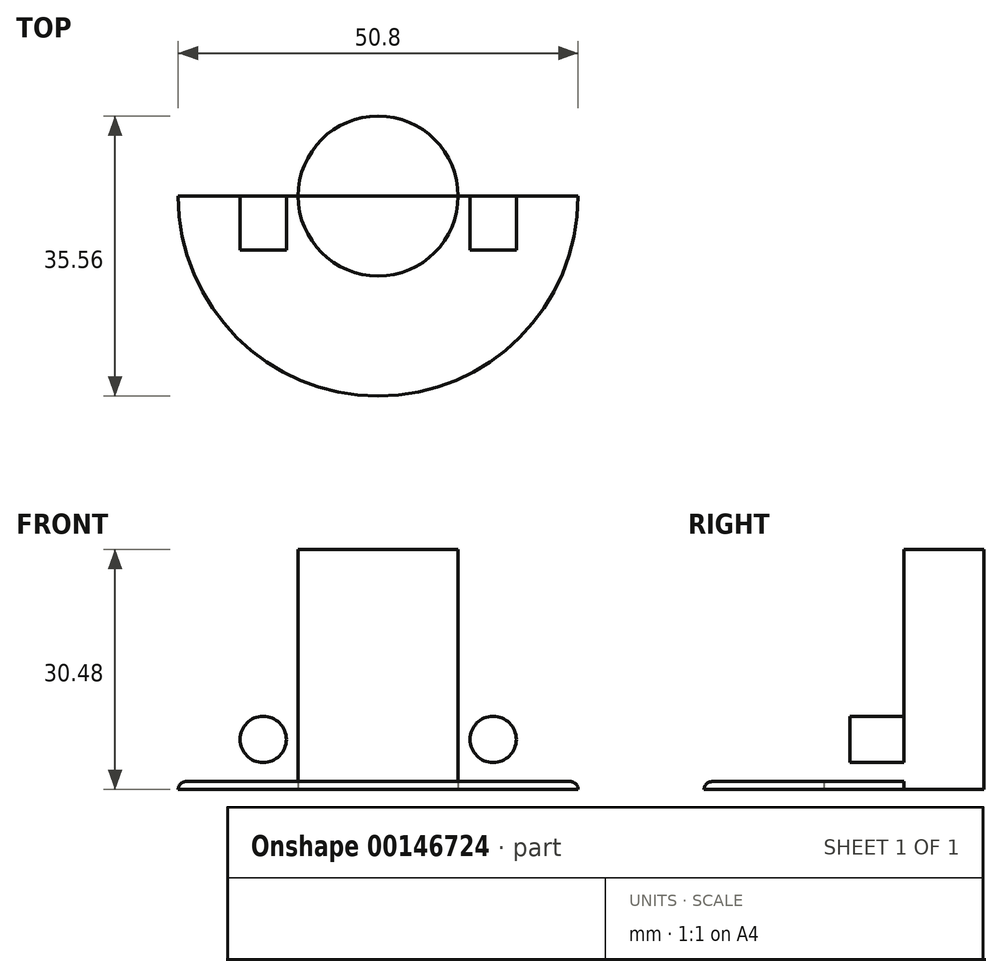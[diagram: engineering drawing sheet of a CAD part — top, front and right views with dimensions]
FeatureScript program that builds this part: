
annotation { "Feature Type Name" : "Feature", "Feature Type Description" : "" }
export const myFeature = defineFeature(function(context is Context, id is Id, definition is map)
    precondition{}
    {
        {
            assignVariable(context, id + "F0", {"name" : "R", "anyValue" : 2});
        }
        {
            var Q0;
            Q0=qCreatedBy(makeId("Top.planeOp"),FACE);
            var sketch = newSketch(context, id + "F1", { "sketchPlane" : qUnion([Q0])});
            skCircle(sketch, "E0", {"center": v(0, 0) * mm, "radius": 25.4 * mm});
            skCircle(sketch, "E1", {"center": v(0, 0) * mm, "radius": 10.16 * mm});
            skLineSegment(sketch, "E2", {"start": v(-25.4, 0) * mm, "end": v(25.4, 0) * mm});
            skSolve(sketch);
        }
        {
            var Q0;
            {var subQ0=sQuery(id+"F1.wireOp",EDGE,"E2");var subQ1=sQuery(id+"F1.wireOp",EDGE,"E0");var subQ2=makeQuery(id+"F1.imprint","INTERSECT",VERTEX,{"disambiguationData":[OD(0.0)],"derivedFrom":[subQ1,subQ0]});Q0=makeQuery(id+"F1.imprint","IMPRINT",FACE,{"disambiguationData":[TD([[makeQuery(id+"F1.imprint","IMPRINT",EDGE,{"disambiguationData":[TD([[subQ2,1.0]])],"derivedFrom":subQ1}),1.0]])]});}
            var Q1;
            {var subQ0=sQuery(id+"F1.wireOp",EDGE,"E2");var subQ1=sQuery(id+"F1.wireOp",EDGE,"E1");var subQ2=makeQuery(id+"F1.imprint","INTERSECT",VERTEX,{"disambiguationData":[OD(0.0)],"derivedFrom":[subQ1,subQ0]});Q1=makeQuery(id+"F1.imprint","IMPRINT",FACE,{"disambiguationData":[TD([[makeQuery(id+"F1.imprint","IMPRINT",EDGE,{"disambiguationData":[TD([[subQ2,1.0]])],"derivedFrom":subQ1}),1.0]])]});}
            extrude(context, id + "F2", {"entities" : qUnion([Q0, Q1]), "depth" : (getVariable(context, 'R') / 2) * mm});
        }
        {
            var Q0;
            Q0=makeQuery(id+"F2.opExtrude","CAP_EDGE",EDGE,{"disambiguationData":[OSD([sQuery(id+"F1.wireOp",EDGE,"E0")])],"isStart":false});
            fillet(context, id + "F3", {"entities" : qUnion([Q0]), "radius" : (getVariable(context, 'R') / 2) * mm, "tangentPropagation" : true, "allowEdgeOverflow" : false});
        }
        {
            var Q0;
            {var subQ0=sQuery(id+"F1.wireOp",EDGE,"E2");var subQ1=sQuery(id+"F1.wireOp",EDGE,"E1");var subQ2=makeQuery(id+"F1.imprint","INTERSECT",VERTEX,{"disambiguationData":[OD(0.0)],"derivedFrom":[subQ1,subQ0]});Q0=makeQuery(id+"F1.imprint","IMPRINT",FACE,{"disambiguationData":[TD([[makeQuery(id+"F1.imprint","IMPRINT",EDGE,{"disambiguationData":[TD([[subQ2,1.0]])],"derivedFrom":subQ1}),1.0]])]});}
            extrude(context, id + "F4", {"entities" : qUnion([Q0]), "operationType" : NewBodyOperationType.ADD, "depth" : 30.48 * mm});
        }
        {
            var Q0;
            Q0=makeQuery(id+"F2.opExtrude","CAP_FACE",FACE,{"disambiguationData":[OSD([sQuery(id+"F1.wireOp",EDGE,"E0"),sQuery(id+"F1.wireOp",EDGE,"E2")])],"isStart":true});
            var sketch = newSketch(context, id + "F5", { "sketchPlane" : qUnion([Q0])});
            skPoint(sketch, "E3", {"position": v(0, 0) * mm});
            skCircle(sketch, "E4", {"center": v(0, 0) * mm, "radius": 6.35 * mm});
            skLineSegment(sketch, "E5", {"start": v(0, 0) * mm, "end": v(-12.7, 0) * mm});
            skLineSegment(sketch, "E6", {"start": v(0, 0) * mm, "end": v(12.7, 0) * mm});
            skCircle(sketch, "E7", {"center": v(-12.7, 0) * mm, "radius": 2.54 * mm});
            skCircle(sketch, "E8", {"center": v(12.7, 0) * mm, "radius": 2.54 * mm});
            skCircle(sketch, "E9", {"center": v(0, 0) * mm, "radius": 3.18 * mm});
            skCircle(sketch, "E10", {"center": v(0, 0) * mm, "radius": 8.26 * mm});
            skSolve(sketch);
        }
        {
            var Q0;
            Q0=sQuery(id+"F5.wireOp",VERTEX,"E3");
            var Q1;
            Q1=makeQuery(id+"F2.opExtrude","SWEPT_BODY",BODY,{"disambiguationData":[OSD([sQuery(id+"F1.wireOp",EDGE,"E0")])]});
            hole(context, id + "F6", {"style" : HoleStyle.SIMPLE, "endStyle" : HoleEndStyle.THROUGH, "holeDiameter" : 16.5 * mm, "startFromSketch" : true, "locations" : qUnion([Q0]), "scope" : qUnion([Q1]), "isTappedThrough" : true});
        }
        {
            var Q0;
            {var subQ0=sQuery(id+"F5.wireOp",EDGE,"E5");var subQ1=sQuery(id+"F5.wireOp",EDGE,"E4");var subQ2=makeQuery(id+"F5.imprint","INTERSECT",VERTEX,{"derivedFrom":[subQ1,subQ0]});Q0=makeQuery(id+"F5.imprint","IMPRINT",FACE,{"disambiguationData":[TD([[makeQuery(id+"F5.imprint","IMPRINT",EDGE,{"disambiguationData":[TD([[subQ2,-1.0]])],"derivedFrom":subQ1}),1.0]])]});}
            var Q1;
            {var subQ0=sQuery(id+"F5.wireOp",EDGE,"E5");var subQ1=sQuery(id+"F5.wireOp",EDGE,"E4");var subQ2=makeQuery(id+"F5.imprint","INTERSECT",VERTEX,{"derivedFrom":[subQ1,subQ0]});Q1=makeQuery(id+"F5.imprint","IMPRINT",FACE,{"disambiguationData":[TD([[makeQuery(id+"F5.imprint","IMPRINT",EDGE,{"disambiguationData":[TD([[subQ2,-1.0]])],"derivedFrom":subQ1}),-1.0]])]});}
            extrude(context, id + "F7", {"entities" : qUnion([Q0, Q1]), "operationType" : NewBodyOperationType.ADD, "oppositeDirection" : true, "depth" : 12.7 * mm});
        }
        {
            var Q0;
            {var subQ0=sQuery(id+"F5.wireOp",EDGE,"E5");var subQ1=sQuery(id+"F5.wireOp",EDGE,"E4");var subQ2=makeQuery(id+"F5.imprint","INTERSECT",VERTEX,{"derivedFrom":[subQ1,subQ0]});Q0=makeQuery(id+"F5.imprint","IMPRINT",FACE,{"disambiguationData":[TD([[makeQuery(id+"F5.imprint","IMPRINT",EDGE,{"disambiguationData":[TD([[subQ2,-1.0]])],"derivedFrom":subQ1}),-1.0]])]});}
            extrude(context, id + "F8", {"entities" : qUnion([Q0]), "operationType" : NewBodyOperationType.ADD, "oppositeDirection" : true, "depth" : 30.48 * mm, "hasSecondDirection" : true, "secondDirectionOppositeDirection" : true, "secondDirectionDepth" : 27.94 * mm});
        }
        {
            var Q0;
            {var subQ0=sQuery(id+"F5.wireOp",EDGE,"E5");var subQ1=sQuery(id+"F1.wireOp",EDGE,"E2");Q0=makeQuery(id+"F8.boolean.opBoolean","MERGE",FACE,{"derivedFrom":[makeQuery(id+"F7.boolean.opBoolean","MERGE",FACE,{"derivedFrom":[makeQuery(id+"F6.hole-0.boolean.opBoolean","SPLIT",FACE,{"disambiguationData":[OD(0.0)],"derivedFrom":makeQuery(id+"F4.boolean.opBoolean","MERGE",FACE,{"derivedFrom":[makeQuery(id+"F2.opExtrude","SWEPT_FACE",FACE,{"disambiguationData":[OSD([subQ1])]}),makeQuery(id+"F4.opExtrude","SWEPT_FACE",FACE,{"disambiguationData":[OSD([subQ1])]})]})}),makeQuery(id+"F7.opExtrude","SWEPT_FACE",FACE,{"disambiguationData":[OSD([subQ0])]})]}),makeQuery(id+"F8.opExtrude","SWEPT_FACE",FACE,{"disambiguationData":[OSD([subQ0])]})]});}
            var sketch = newSketch(context, id + "F11", { "sketchPlane" : qUnion([Q0])});
            skLineSegment(sketch, "E11", {"start": v(-8.26, 12.7) * mm, "end": v(-8.26, 6.35) * mm});
            skLineSegment(sketch, "E12", {"start": v(-8.26, 6.35) * mm, "end": v(-8.26, 0) * mm});
            skLineSegment(sketch, "E13", {"start": v(-8.26, 6.35) * mm, "end": v(-14.6, 6.35) * mm});
            skLineSegment(sketch, "E14", {"start": v(-14.6, 6.35) * mm, "end": v(-8.26, 12.7) * mm});
            skCircle(sketch, "E15", {"center": v(-14.6, 6.35) * mm, "radius": 2.94 * mm});
            skSolve(sketch);
        }
        {
            var Q0;
            {var subQ0=sQuery(id+"F5.wireOp",EDGE,"E6");var subQ1=sQuery(id+"F1.wireOp",EDGE,"E2");Q0=makeQuery(id+"F8.boolean.opBoolean","MERGE",FACE,{"derivedFrom":[makeQuery(id+"F7.boolean.opBoolean","MERGE",FACE,{"derivedFrom":[makeQuery(id+"F6.hole-0.boolean.opBoolean","SPLIT",FACE,{"disambiguationData":[OD(1.0)],"derivedFrom":makeQuery(id+"F4.boolean.opBoolean","MERGE",FACE,{"derivedFrom":[makeQuery(id+"F2.opExtrude","SWEPT_FACE",FACE,{"disambiguationData":[OSD([subQ1])]}),makeQuery(id+"F4.opExtrude","SWEPT_FACE",FACE,{"disambiguationData":[OSD([subQ1])]})]})}),makeQuery(id+"F7.opExtrude","SWEPT_FACE",FACE,{"disambiguationData":[OSD([subQ0])]})]}),makeQuery(id+"F8.opExtrude","SWEPT_FACE",FACE,{"disambiguationData":[OSD([subQ0])]})]});}
            var sketch = newSketch(context, id + "F9", { "sketchPlane" : qUnion([Q0])});
            skLineSegment(sketch, "E16", {"start": v(8.26, 12.7) * mm, "end": v(8.26, 6.35) * mm});
            skLineSegment(sketch, "E17", {"start": v(8.26, 6.35) * mm, "end": v(8.26, 0) * mm});
            skLineSegment(sketch, "E18", {"start": v(8.26, 0) * mm, "end": v(8.26, 0) * mm});
            skLineSegment(sketch, "E19", {"start": v(8.26, 6.35) * mm, "end": v(14.6, 6.35) * mm});
            skLineSegment(sketch, "E20", {"start": v(8.26, 12.7) * mm, "end": v(14.6, 6.35) * mm});
            skCircle(sketch, "E21", {"center": v(14.6, 6.35) * mm, "radius": 2.94 * mm});
            skSolve(sketch);
        }
        {
            var Q0;
            {var subQ0=sQuery(id+"F11.wireOp",EDGE,"E14");var subQ1=sQuery(id+"F11.wireOp",EDGE,"E13");var subQ2=makeQuery(id+"F11.imprint","INTERSECT",VERTEX,{"derivedFrom":[subQ1,subQ0]});Q0=makeQuery(id+"F11.imprint","IMPRINT",FACE,{"disambiguationData":[TD([[makeQuery(id+"F11.imprint","IMPRINT",EDGE,{"disambiguationData":[TD([[subQ2,1.0]])],"derivedFrom":subQ1}),1.0]])]});}
            var Q1;
            {var subQ0=sQuery(id+"F11.wireOp",EDGE,"E14");var subQ1=sQuery(id+"F11.wireOp",EDGE,"E13");var subQ2=makeQuery(id+"F11.imprint","INTERSECT",VERTEX,{"derivedFrom":[subQ1,subQ0]});Q1=makeQuery(id+"F11.imprint","IMPRINT",FACE,{"disambiguationData":[TD([[makeQuery(id+"F11.imprint","IMPRINT",EDGE,{"disambiguationData":[TD([[subQ2,1.0]])],"derivedFrom":subQ1}),-1.0]])]});}
            var Q2;
            {var subQ0=sQuery(id+"F9.wireOp",EDGE,"E20");var subQ1=sQuery(id+"F9.wireOp",EDGE,"E19");var subQ2=makeQuery(id+"F9.imprint","INTERSECT",VERTEX,{"derivedFrom":[subQ1,subQ0]});Q2=makeQuery(id+"F9.imprint","IMPRINT",FACE,{"disambiguationData":[TD([[makeQuery(id+"F9.imprint","IMPRINT",EDGE,{"disambiguationData":[TD([[subQ2,1.0]])],"derivedFrom":subQ1}),1.0]])]});}
            var Q3;
            {var subQ0=sQuery(id+"F9.wireOp",EDGE,"E20");var subQ1=sQuery(id+"F9.wireOp",EDGE,"E19");var subQ2=makeQuery(id+"F9.imprint","INTERSECT",VERTEX,{"derivedFrom":[subQ1,subQ0]});Q3=makeQuery(id+"F9.imprint","IMPRINT",FACE,{"disambiguationData":[TD([[makeQuery(id+"F9.imprint","IMPRINT",EDGE,{"disambiguationData":[TD([[subQ2,1.0]])],"derivedFrom":subQ1}),-1.0]])]});}
            extrude(context, id + "F10", {"entities" : qUnion([Q0, Q1, Q2, Q3]), "operationType" : NewBodyOperationType.ADD, "depth" : 6.86 * mm});
        }
    });
